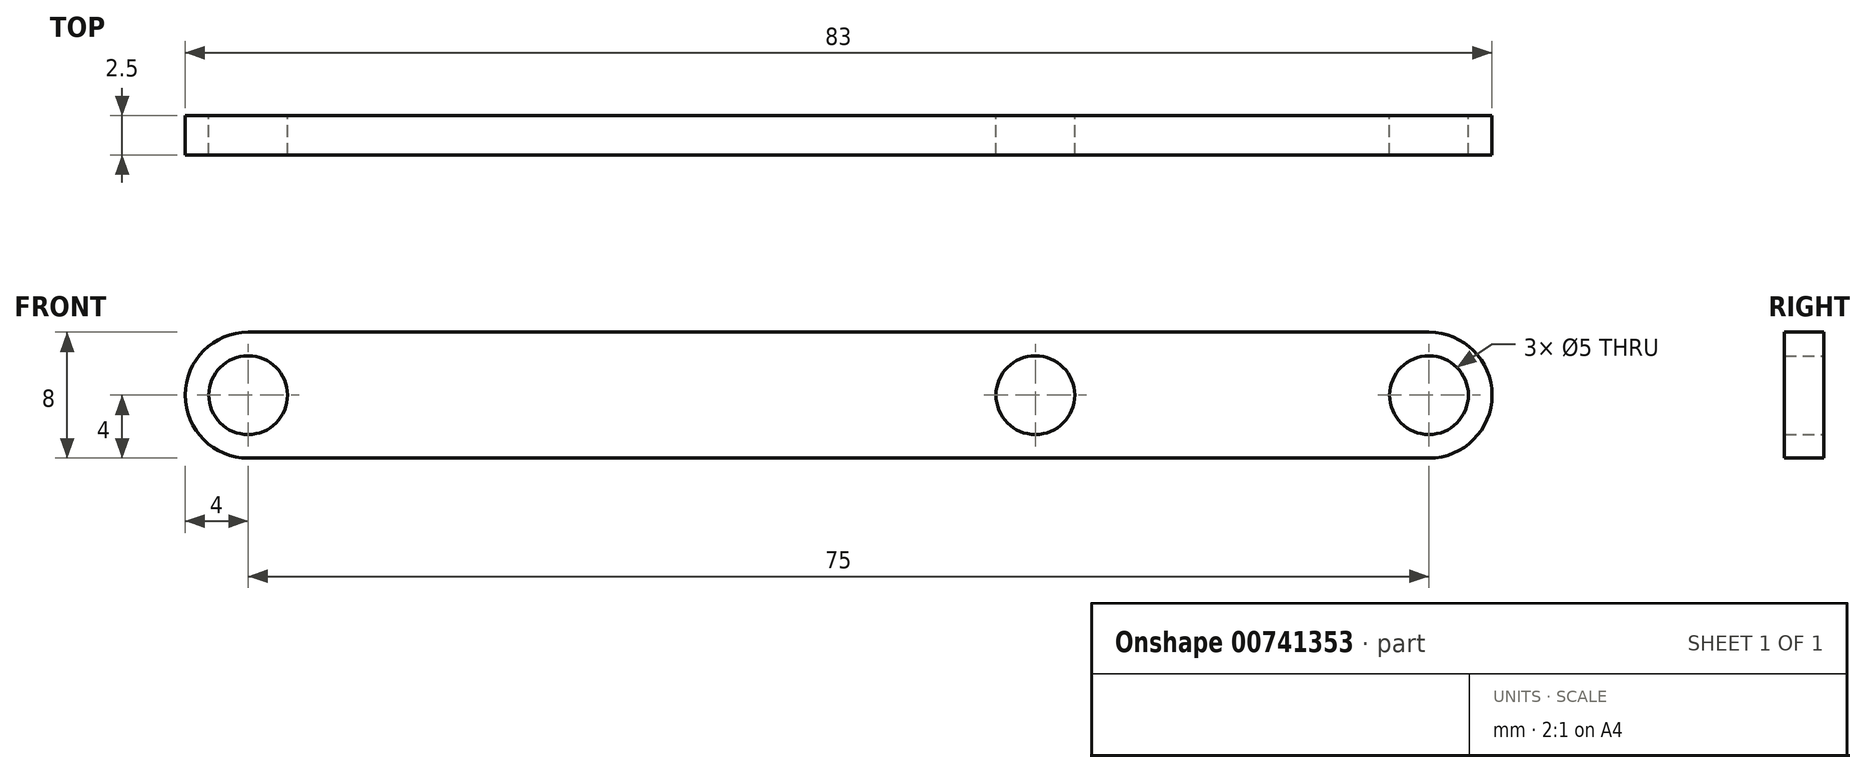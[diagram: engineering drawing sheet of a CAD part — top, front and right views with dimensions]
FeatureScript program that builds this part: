
annotation { "Feature Type Name" : "Feature", "Feature Type Description" : "" }
export const myFeature = defineFeature(function(context is Context, id is Id, definition is map)
    precondition{}
    {
        {
            var Q0;
            Q0=qCreatedBy(makeId("Front.planeOp"),FACE);
            var sketch = newSketch(context, id + "F0", { "sketchPlane" : qUnion([Q0])});
            skArc(sketch, "E0", {"start": v(0, 4) * mm, "mid": v(-4, 0) * mm, "end": v(0, -4) * mm});
            skCircle(sketch, "E1", {"center": v(0, 0) * mm, "radius": 2.5 * mm});
            skLineSegment(sketch, "E2", {"start": v(0, 0) * mm, "end": v(75, 0) * mm, "construction": true});
            skArc(sketch, "E3", {"start": v(75, -4) * mm, "mid": v(79, 0) * mm, "end": v(75, 4) * mm});
            skCircle(sketch, "E4", {"center": v(75, 0) * mm, "radius": 2.5 * mm});
            skLineSegment(sketch, "E5.0", {"start": v(0, -4) * mm, "end": v(75, -4) * mm});
            skLineSegment(sketch, "E6.0", {"start": v(0, 4) * mm, "end": v(75, 4) * mm});
            skCircle(sketch, "E7", {"center": v(50, 0) * mm, "radius": 2.5 * mm});
            skSolve(sketch);
        }
        {
            var Q0;
            Q0 = qSketchRegion(id + "F0", true);
            extrude(context, id + "F1", {"entities" : qUnion([Q0]), "depth" : 2.5 * mm, "offsetDistance" : 25 * mm});
        }
    });
